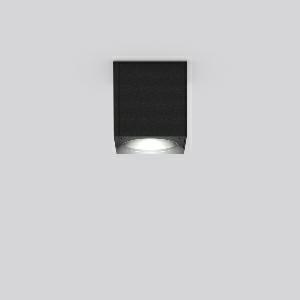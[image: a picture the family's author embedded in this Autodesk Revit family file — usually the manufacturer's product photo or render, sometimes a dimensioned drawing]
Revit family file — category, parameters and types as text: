
# Revit family: hb_111_931187_0031_80df
name_source: partatom
category: Lighting Fixtures
units: mm (PartAtom-declared; Revit-internal decimal feet)

## family parameters
Cut with Voids When Loaded = No
Host = Face
Light Source = No
Part Type = Normal
Room Calculation Point = No
Round Connector Dimension = Use Diameter
Shared = No

## types (1)
- HB 111 (1 x LED Modul 830, 590 lm, 3000)
    Apparent Load = 9 VA
    CIE Flux Codes = 64 91 96 87 100
    Color Rendering = 80
    Color Temperature = 3000
    Default Elevation = 1800 mm
    Description = Series: HB 111
Square surface-mounted downlight for outdoor use. Housing: die-cast aluminium, powder-coated. Clear glass cover. Driver integrated. 
Colour: anthracite metallic (DB703)
Length: 90 mm
Width: 90 mm
Height: 94 mm
Lamp: LED
System power: 9 W
Rated luminous flux: 590 lm
Luminous efficiency: 66 lm/W
Control gear: Regulated power supply
Protection class: I
Type of protection: IP 54
    Height = 94 mm  [stored 0.308399 ft]
    Lamp = 1 x LED Modul 830
    Lamp Light Flux = 590 lm
    Lamp count = 1
    Length = 90 mm
    Lifetime = 50000 h
    Luminous efficacy = 66 lm/W
    Manufacturer = RZB
    ModVariant = No
    Model = 931187.0031
    Mounting Place = Ceiling
    Mounting Type = Surface mounted
    Number of Poles = 1
    OnlyDefault = Yes
    Power Factor = 1
    Product Name = HB 111
    Product group = Surface mounted ceiling luminaires
    ProductGroupID = 303
    Protection Class = Protection class I
    Protection Degree = IP 54
    RLX_Detail_Level = 1
    RLX_Emergency_Light_Flux = 0 lm
    RLX_Emergency_Type = 0
    RLX_Emergency_Type_DB = No
    RlxData = <blob elided: 23153 chars, md5=1701a2c7>
    Socket = socket
    Standby Power = 0 W
    System Light Flux = 590 lm
    System Power = 9 W
    Type Comments = ALEA SPOT
    Type Image = 931187.0031.jpg
    URL = http://relux.com
    VarID = ---
    Voltage = 230 V
    Voltage Range = 220-240 V
    Weight = 0.00 kg
    Width = 90 mm

note: [stored X ft] marks values corroborated as IEEE doubles in the binary element streams (Revit-internal decimal feet)

## geometry (parser evidence)
native form markers: Blend x4, Sweep x12
no freeform markers — native parametric forms only
